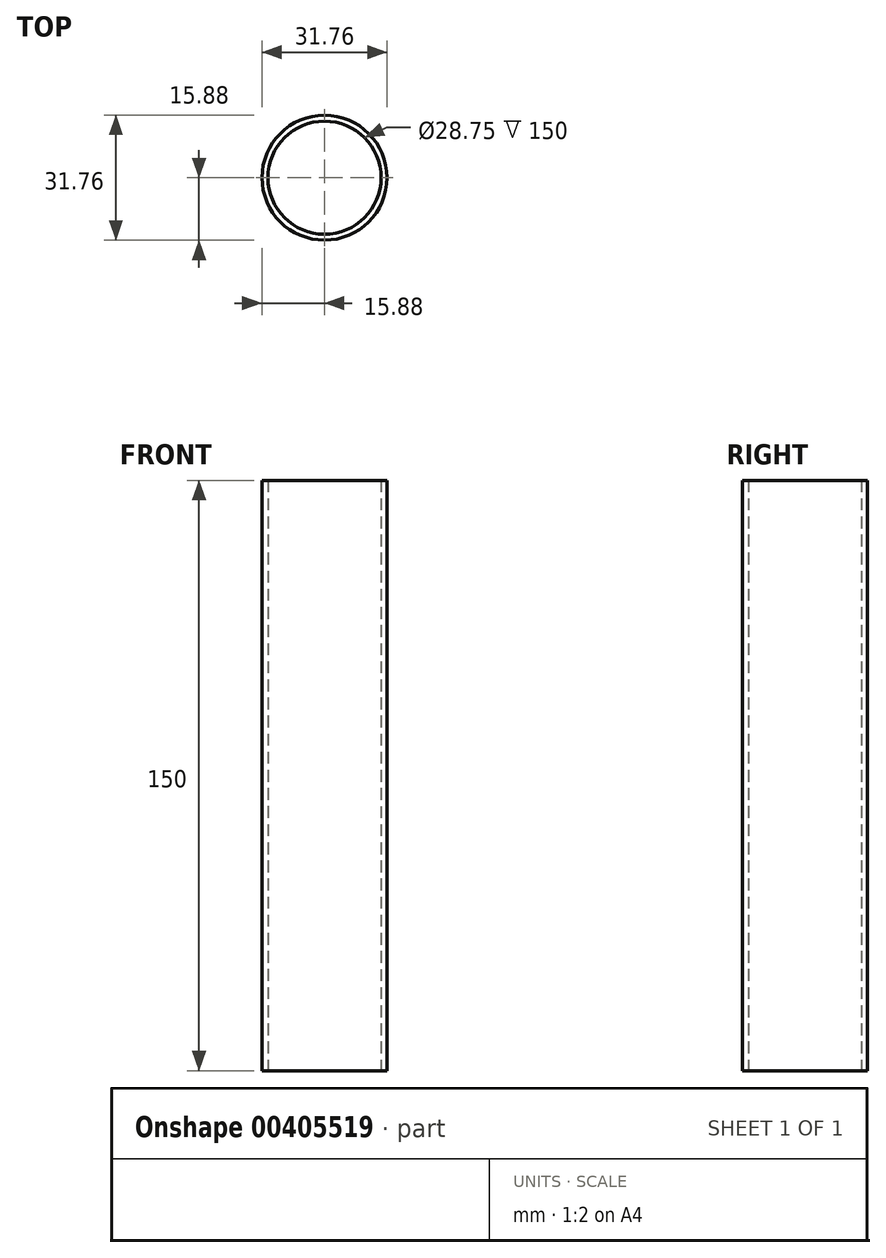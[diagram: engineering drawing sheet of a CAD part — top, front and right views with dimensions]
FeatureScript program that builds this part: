
annotation { "Feature Type Name" : "Feature", "Feature Type Description" : "" }
export const myFeature = defineFeature(function(context is Context, id is Id, definition is map)
    precondition{}
    {
        {
            var Q0;
            Q0=qCreatedBy(makeId("Top.planeOp"),FACE);
            var sketch = newSketch(context, id + "F0", { "sketchPlane" : qUnion([Q0])});
            skPoint(sketch, "E0.middle", {"position": v(0, 0) * mm});
            skCircle(sketch, "E1", {"center": v(0, 0) * mm, "radius": 15.88 * mm});
            skCircle(sketch, "E2.0", {"center": v(0, 0) * mm, "radius": 14.38 * mm});
            skSolve(sketch);
        }
        {
            var Q0;
            Q0=makeQuery(id+"F0.imprint","IMPRINT",FACE,{"disambiguationData":[TD([[makeQuery(id+"F0.imprint","IMPRINT",EDGE,{"derivedFrom":sQuery(id+"F0.wireOp",EDGE,"E1")}),1.0]])]});
            extrude(context, id + "F1", {"entities" : qUnion([Q0]), "depth" : 150 * mm});
        }
    });
